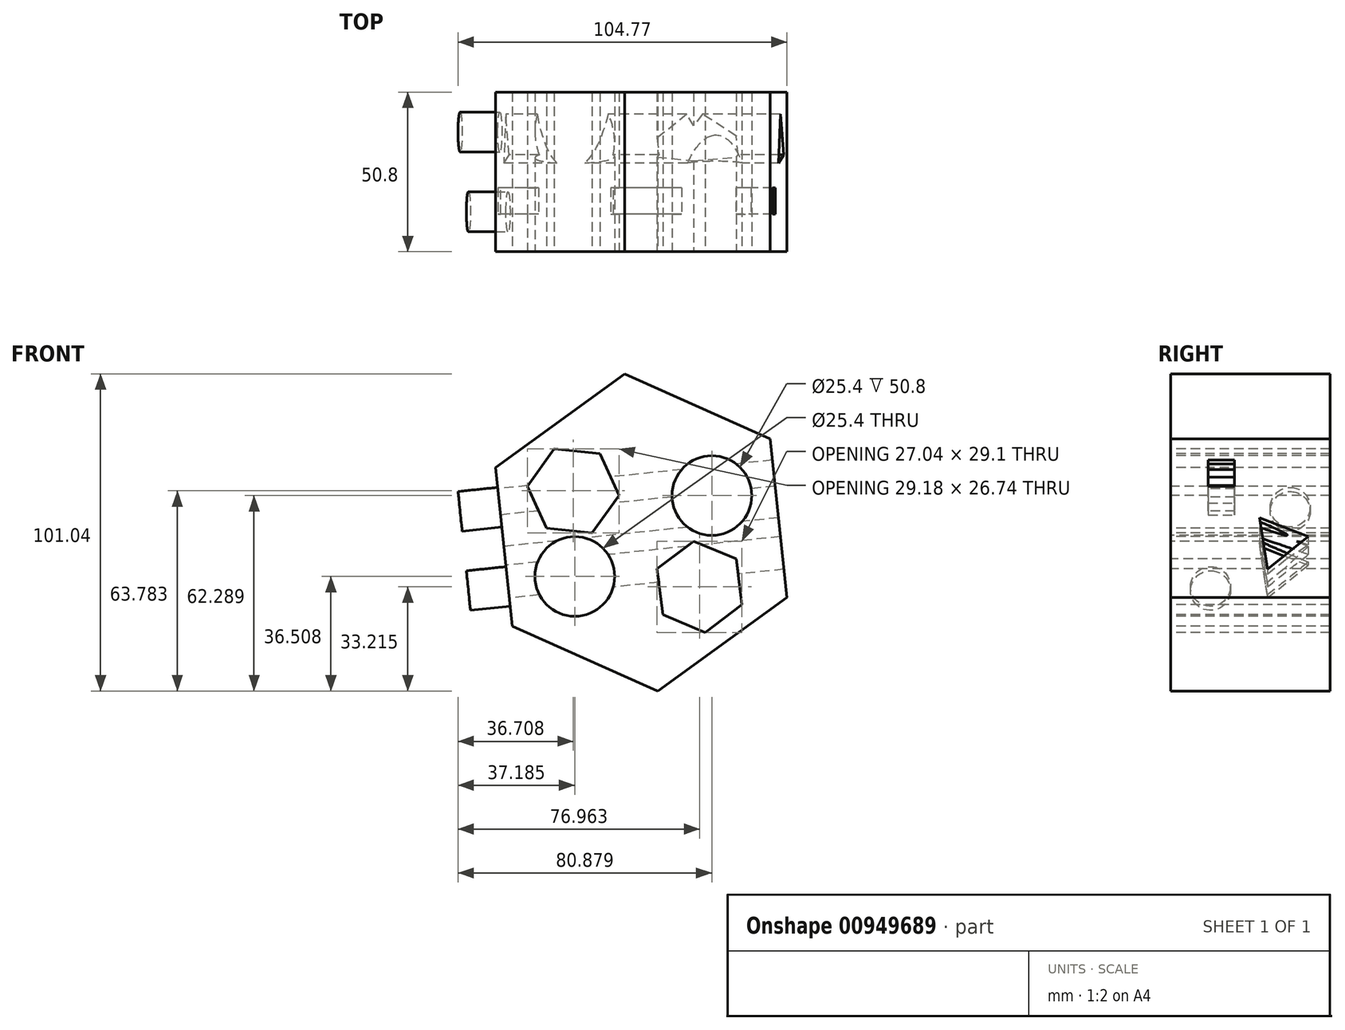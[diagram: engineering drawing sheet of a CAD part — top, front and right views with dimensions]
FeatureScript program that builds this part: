
annotation { "Feature Type Name" : "Feature", "Feature Type Description" : "" }
export const myFeature = defineFeature(function(context is Context, id is Id, definition is map)
    precondition{}
    {
        {
            var Q0;
            Q0=qCreatedBy(makeId("Front.planeOp"),FACE);
            var sketch = newSketch(context, id + "F0", { "sketchPlane" : qUnion([Q0])});
            skCircle(sketch, "E0.cCircle", {"center": v(0, 0) * mm, "radius": 44 * mm, "construction": true});
            skLineSegment(sketch, "E0.0", {"start": v(46.4, -20.69) * mm, "end": v(5.28, -50.52) * mm});
            skLineSegment(sketch, "E0.1", {"start": v(5.28, -50.52) * mm, "end": v(-41.11, -29.84) * mm});
            skLineSegment(sketch, "E0.2", {"start": v(-41.11, -29.84) * mm, "end": v(-46.4, 20.69) * mm});
            skLineSegment(sketch, "E0.3", {"start": v(-46.4, 20.69) * mm, "end": v(-5.28, 50.52) * mm});
            skLineSegment(sketch, "E0.4", {"start": v(-5.28, 50.52) * mm, "end": v(41.11, 29.84) * mm});
            skLineSegment(sketch, "E0.5", {"start": v(41.11, 29.84) * mm, "end": v(46.4, -20.69) * mm});
            skPoint(sketch, "E0.0.midPoint", {"position": v(25.84, -35.6) * mm});
            skPoint(sketch, "E1", {"position": v(-21.66, 13.26) * mm});
            skPoint(sketch, "E2", {"position": v(18.6, -17.3) * mm});
            skCircle(sketch, "E3", {"center": v(-21.19, -14.01) * mm, "radius": 12.7 * mm});
            skCircle(sketch, "E4", {"center": v(22.5, 11.77) * mm, "radius": 12.7 * mm});
            skCircle(sketch, "E5.cCircle", {"center": v(-21.66, 13.26) * mm, "radius": 12.7 * mm, "construction": true});
            skLineSegment(sketch, "E5.0", {"start": v(-7.07, 11.8) * mm, "end": v(-15.64, -0.1) * mm});
            skLineSegment(sketch, "E5.1", {"start": v(-15.64, -0.1) * mm, "end": v(-30.23, 1.36) * mm});
            skLineSegment(sketch, "E5.2", {"start": v(-30.23, 1.36) * mm, "end": v(-36.25, 14.73) * mm});
            skLineSegment(sketch, "E5.3", {"start": v(-36.25, 14.73) * mm, "end": v(-27.69, 26.63) * mm});
            skLineSegment(sketch, "E5.4", {"start": v(-27.69, 26.63) * mm, "end": v(-13.1, 25.17) * mm});
            skLineSegment(sketch, "E5.5", {"start": v(-13.1, 25.17) * mm, "end": v(-7.07, 11.8) * mm});
            skPoint(sketch, "E5.0.midPoint", {"position": v(-11.35, 5.84) * mm});
            skCircle(sketch, "E6.cCircle", {"center": v(18.6, -17.3) * mm, "radius": 12.7 * mm, "construction": true});
            skLineSegment(sketch, "E6.0", {"start": v(32.12, -22.98) * mm, "end": v(20.44, -31.85) * mm});
            skLineSegment(sketch, "E6.1", {"start": v(20.44, -31.85) * mm, "end": v(6.92, -26.18) * mm});
            skLineSegment(sketch, "E6.2", {"start": v(6.92, -26.18) * mm, "end": v(5.07, -11.63) * mm});
            skLineSegment(sketch, "E6.3", {"start": v(5.07, -11.63) * mm, "end": v(16.75, -2.76) * mm});
            skLineSegment(sketch, "E6.4", {"start": v(16.75, -2.76) * mm, "end": v(30.27, -8.43) * mm});
            skLineSegment(sketch, "E6.5", {"start": v(30.27, -8.43) * mm, "end": v(32.12, -22.98) * mm});
            skPoint(sketch, "E6.0.midPoint", {"position": v(26.28, -27.42) * mm});
            skPoint(sketch, "E7.1.0", {"position": v(-0.65, -25.4) * mm});
            skPoint(sketch, "E7.2.0", {"position": v(22.32, 12.13) * mm});
            skPoint(sketch, "E8.1.0", {"position": v(5.69, 24.75) * mm});
            skPoint(sketch, "E8.2.0", {"position": v(-24.28, -7.45) * mm});
            skLineSegment(sketch, "E9.anchor1", {"start": v(0, 0) * mm, "end": v(-21.66, 13.26) * mm, "construction": true});
            skLineSegment(sketch, "E9.anchor2", {"start": v(0, 0) * mm, "end": v(-0.65, -25.4) * mm, "construction": true});
            skSolve(sketch);
        }
        {
            var Q0;
            Q0=makeQuery(id+"F0.imprint","IMPRINT",FACE,{"disambiguationData":[TD([[makeQuery(id+"F0.imprint","IMPRINT",EDGE,{"derivedFrom":sQuery(id+"F0.wireOp",EDGE,"E0.0")}),-1.0]])]});
            extrude(context, id + "F1", {"entities" : qUnion([Q0]), "endBound" : BoundingType.SYMMETRIC, "oppositeDirection" : true, "depth" : 50.8 * mm, "offsetDistance" : 25.4 * mm});
        }
        {
            var Q0;
            Q0=makeQuery(id+"F1.opExtrude","SWEPT_FACE",FACE,{"disambiguationData":[OSD([sQuery(id+"F0.wireOp",EDGE,"E0.2")])]});
            var sketch = newSketch(context, id + "F2", { "sketchPlane" : qUnion([Q0])});
            skCircle(sketch, "E10.cCircle", {"center": v(-8.9, -7.39) * mm, "radius": 4.83 * mm, "construction": true});
            skLineSegment(sketch, "E10.0", {"start": v(-5.4, -16.39) * mm, "end": v(-18.44, -5.92) * mm});
            skLineSegment(sketch, "E10.1", {"start": v(-18.44, -5.92) * mm, "end": v(-2.85, 0.14) * mm});
            skLineSegment(sketch, "E10.2", {"start": v(-2.85, 0.14) * mm, "end": v(-5.4, -16.39) * mm});
            skPoint(sketch, "E10.0.midPoint", {"position": v(-11.92, -11.15) * mm});
            skCircle(sketch, "E11.cCircle", {"center": v(9.23, 14.43) * mm, "radius": 4.19 * mm, "construction": true});
            skLineSegment(sketch, "E11.0", {"start": v(13.42, 10.24) * mm, "end": v(5.04, 10.24) * mm});
            skLineSegment(sketch, "E11.1", {"start": v(5.04, 10.24) * mm, "end": v(5.04, 18.62) * mm});
            skLineSegment(sketch, "E11.2", {"start": v(5.04, 18.62) * mm, "end": v(13.42, 18.62) * mm});
            skLineSegment(sketch, "E11.3", {"start": v(13.42, 18.62) * mm, "end": v(13.42, 10.24) * mm});
            skPoint(sketch, "E11.0.midPoint", {"position": v(9.23, 10.24) * mm});
            skSolve(sketch);
        }
        {
            var Q0;
            Q0=makeQuery(id+"F2.imprint","IMPRINT",FACE,{"disambiguationData":[TD([[makeQuery(id+"F2.imprint","IMPRINT",EDGE,{"derivedFrom":sQuery(id+"F2.wireOp",EDGE,"E11.0")}),-1.0]])]});
            var Q1;
            Q1=makeQuery(id+"F2.imprint","IMPRINT",FACE,{"disambiguationData":[TD([[makeQuery(id+"F2.imprint","IMPRINT",EDGE,{"derivedFrom":sQuery(id+"F2.wireOp",EDGE,"E10.0")}),-1.0]])]});
            extrude(context, id + "F3", {"entities" : qUnion([Q0, Q1]), "operationType" : NewBodyOperationType.REMOVE, "endBound" : BoundingType.THROUGH_ALL, "oppositeDirection" : true, "depth" : 25.4 * mm, "offsetDistance" : 25.4 * mm});
        }
        {
            var Q0;
            Q0=makeQuery(id+"F1.opExtrude","SWEPT_FACE",FACE,{"disambiguationData":[OSD([sQuery(id+"F0.wireOp",EDGE,"E0.2")])]});
            var sketch = newSketch(context, id + "F4", { "sketchPlane" : qUnion([Q0])});
            skCircle(sketch, "E12", {"center": v(12.7, -12.7) * mm, "radius": 6.35 * mm});
            skCircle(sketch, "E13", {"center": v(-12.7, 12.7) * mm, "radius": 6.35 * mm});
            skSolve(sketch);
        }
        {
            var Q0;
            Q0=makeQuery(id+"F4.imprint","IMPRINT",FACE,{"disambiguationData":[TD([[makeQuery(id+"F4.imprint","IMPRINT",EDGE,{"derivedFrom":sQuery(id+"F4.wireOp",EDGE,"E13")}),1.0]])]});
            var Q1;
            Q1=makeQuery(id+"F4.imprint","IMPRINT",FACE,{"disambiguationData":[TD([[makeQuery(id+"F4.imprint","IMPRINT",EDGE,{"derivedFrom":sQuery(id+"F4.wireOp",EDGE,"E12")}),1.0]])]});
            extrude(context, id + "F5", {"entities" : qUnion([Q0, Q1]), "depth" : 12.7 * mm, "offsetDistance" : 25.4 * mm});
        }
    });
